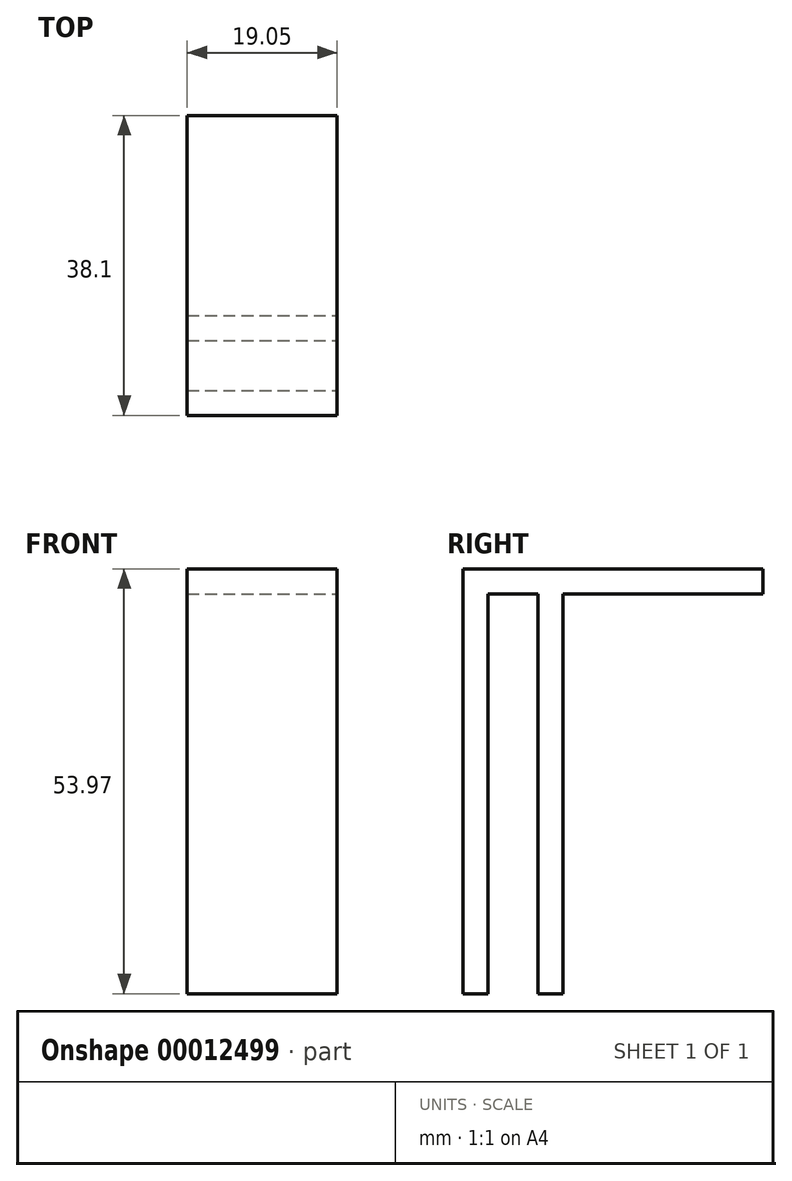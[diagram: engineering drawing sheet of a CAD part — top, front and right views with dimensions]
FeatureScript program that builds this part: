
annotation { "Feature Type Name" : "Feature", "Feature Type Description" : "" }
export const myFeature = defineFeature(function(context is Context, id is Id, definition is map)
    precondition{}
    {
        {
            var Q0;
            Q0=qCreatedBy(makeId("Top.planeOp"),FACE);
            var sketch = newSketch(context, id + "F0", { "sketchPlane" : qUnion([Q0])});
            skLineSegment(sketch, "E0.bottom", {"start": v(0, 0) * mm, "end": v(19.05, 0) * mm});
            skLineSegment(sketch, "E0.top", {"start": v(0, 38.1) * mm, "end": v(19.05, 38.1) * mm});
            skLineSegment(sketch, "E0.left", {"start": v(0, 0) * mm, "end": v(0, 38.1) * mm});
            skLineSegment(sketch, "E0.right", {"start": v(19.05, 0) * mm, "end": v(19.05, 38.1) * mm});
            skSolve(sketch);
        }
        {
            var Q0;
            Q0 = qSketchRegion(id + "F0", true);
            extrude(context, id + "F1", {"entities" : qUnion([Q0]), "depth" : 3.17 * mm});
        }
        {
            var Q0;
            Q0=qCreatedBy(makeId("Top.planeOp"),FACE);
            var sketch = newSketch(context, id + "F2", { "sketchPlane" : qUnion([Q0])});
            skLineSegment(sketch, "E1.bottom", {"start": v(0, 0) * mm, "end": v(19.05, 0) * mm});
            skLineSegment(sketch, "E1.top", {"start": v(0, 3.18) * mm, "end": v(19.05, 3.18) * mm});
            skLineSegment(sketch, "E1.left", {"start": v(0, 0) * mm, "end": v(0, 3.18) * mm});
            skLineSegment(sketch, "E1.right", {"start": v(19.05, 0) * mm, "end": v(19.05, 3.18) * mm});
            skLineSegment(sketch, "E2", {"start": v(0, 9.52) * mm, "end": v(19.02, 9.52) * mm});
            skLineSegment(sketch, "E3.bottom", {"start": v(0, 9.52) * mm, "end": v(19.05, 9.52) * mm});
            skLineSegment(sketch, "E3.top", {"start": v(0, 12.7) * mm, "end": v(19.05, 12.7) * mm});
            skLineSegment(sketch, "E3.left", {"start": v(0, 9.52) * mm, "end": v(0, 12.7) * mm});
            skLineSegment(sketch, "E3.right", {"start": v(19.05, 9.52) * mm, "end": v(19.05, 12.7) * mm});
            skSolve(sketch);
        }
        {
            var Q0;
            Q0=makeQuery(id+"F2.imprint","IMPRINT",FACE,{"disambiguationData":[TD([[makeQuery(id+"F2.imprint","IMPRINT",EDGE,{"derivedFrom":sQuery(id+"F2.wireOp",EDGE,"E1.bottom")}),1.0]])]});
            var Q1;
            Q1=makeQuery(id+"F2.imprint","IMPRINT",FACE,{"disambiguationData":[TD([[makeQuery(id+"F2.imprint","IMPRINT",EDGE,{"derivedFrom":sQuery(id+"F2.wireOp",EDGE,"E3.top")}),-1.0]])]});
            extrude(context, id + "F3", {"entities" : qUnion([Q0, Q1]), "operationType" : NewBodyOperationType.ADD, "oppositeDirection" : true, "depth" : 50.8 * mm});
        }
    });
